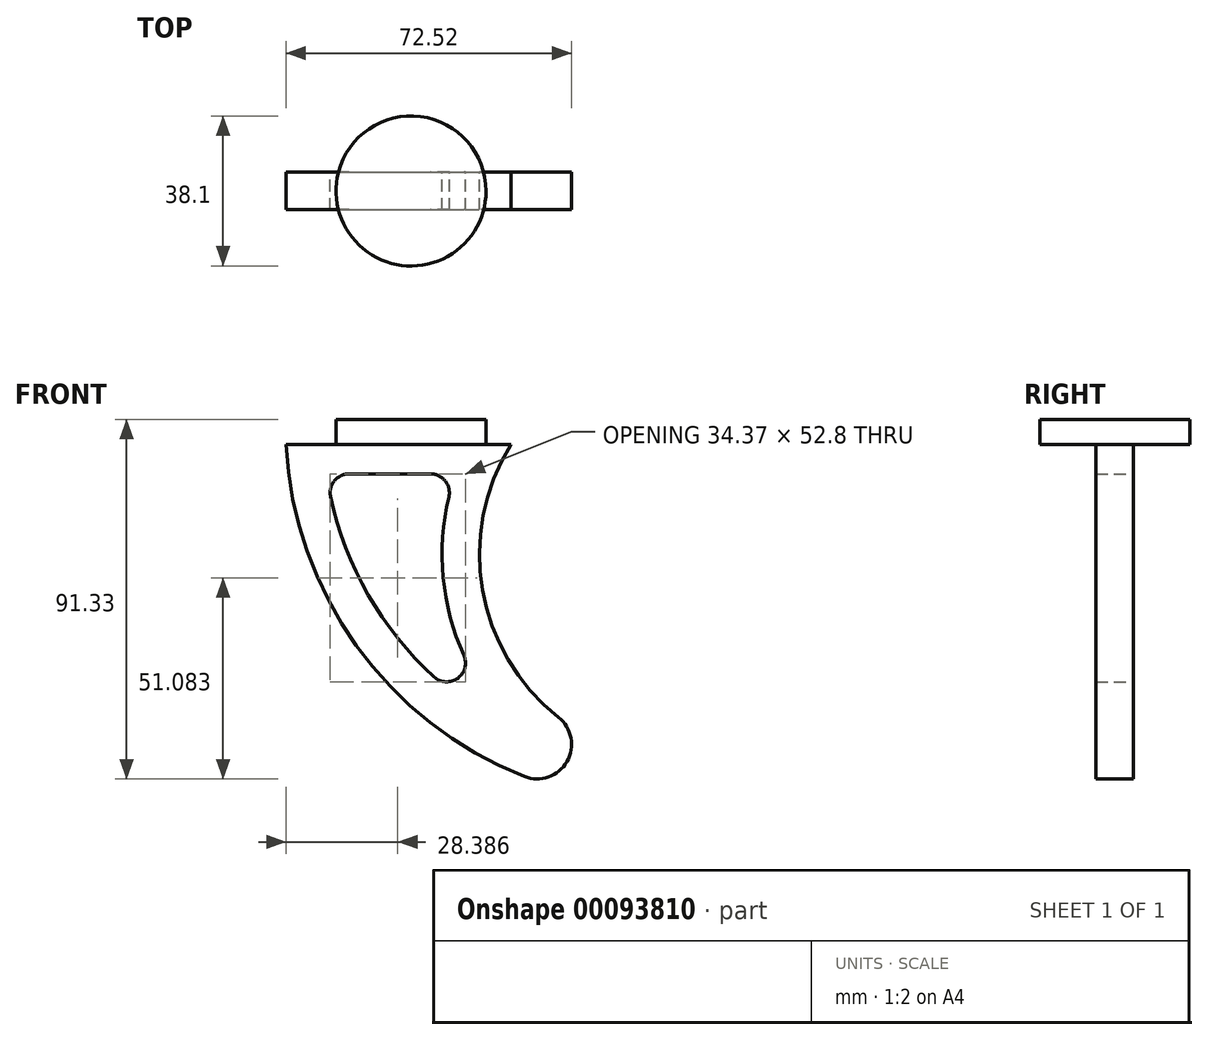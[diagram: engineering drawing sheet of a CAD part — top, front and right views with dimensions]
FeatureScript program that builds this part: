
annotation { "Feature Type Name" : "Feature", "Feature Type Description" : "" }
export const myFeature = defineFeature(function(context is Context, id is Id, definition is map)
    precondition{}
    {
        {
            var Q0;
            Q0=qCreatedBy(makeId("Front.planeOp"),FACE);
            var sketch = newSketch(context, id + "F0", { "sketchPlane" : qUnion([Q0])});
            skLineSegment(sketch, "E0", {"start": v(0, 0) * mm, "end": v(57.15, 0) * mm});
            skArc(sketch, "E1", {"start": v(0, 0) * mm, "mid": v(17.84, -51.1) * mm, "end": v(60.53, -84.37) * mm});
            skArc(sketch, "E2", {"start": v(57.15, 0) * mm, "mid": v(49.94, -36.96) * mm, "end": v(69.2, -69.32) * mm});
            skArc(sketch, "E3", {"start": v(60.53, -84.37) * mm, "mid": v(71.35, -80.58) * mm, "end": v(69.2, -69.32) * mm});
            skLineSegment(sketch, "E4", {"start": v(15.96, -7.5) * mm, "end": v(36.73, -7.5) * mm});
            skArc(sketch, "E5", {"start": v(11.3, -13.25) * mm, "mid": v(20.87, -38.22) * mm, "end": v(37.62, -59.07) * mm});
            skArc(sketch, "E6", {"start": v(41.36, -13.37) * mm, "mid": v(39.91, -33.8) * mm, "end": v(45.16, -53.58) * mm});
            skArc(sketch, "E7", {"start": v(37.62, -59.07) * mm, "mid": v(43.62, -59.4) * mm, "end": v(45.16, -53.58) * mm});
            skPoint(sketch, "E8.visualSharp", {"position": v(10.28, -7.5) * mm});
            skArc(sketch, "E8.filletArc", {"start": v(15.96, -7.5) * mm, "mid": v(12.26, -9.26) * mm, "end": v(11.3, -13.25) * mm});
            skPoint(sketch, "E9.visualSharp", {"position": v(43.08, -7.5) * mm});
            skArc(sketch, "E9.filletArc", {"start": v(41.36, -13.37) * mm, "mid": v(40.47, -9.31) * mm, "end": v(36.73, -7.5) * mm});
            skSolve(sketch);
        }
        {
            var Q0;
            Q0 = qSketchRegion(id + "F0", true);
            extrude(context, id + "F1", {"entities" : qUnion([Q0]), "depth" : 9.52 * mm});
        }
        {
            var Q0;
            Q0=makeQuery(id+"F1.opExtrude","SWEPT_FACE",FACE,{"disambiguationData":[OSD([sQuery(id+"F0.wireOp",EDGE,"E0")])]});
            var sketch = newSketch(context, id + "F2", { "sketchPlane" : qUnion([Q0])});
            skSolve(sketch);
        }
        {
            var Q0;
            {var subQ0=sQuery(id+"F0.wireOp",EDGE,"E0");Q0=makeQuery(id+"F2.imprint","IMPRINT",FACE,{"disambiguationData":[TD([[makeQuery(id+"F2.imprint","IMPRINT",EDGE,{"derivedFrom":makeQuery(id+"F1.opExtrude","CAP_EDGE",EDGE,{"disambiguationData":[OSD([subQ0])],"isStart":true})}),-1.0]])]});}
            var sketch = newSketch(context, id + "F3", { "sketchPlane" : qUnion([Q0])});
            skCircle(sketch, "E10", {"center": v(31.75, -4.76) * mm, "radius": 19.05 * mm});
            skSolve(sketch);
        }
        {
            var Q0;
            Q0 = qSketchRegion(id + "F3", true);
            extrude(context, id + "F4", {"entities" : qUnion([Q0]), "operationType" : NewBodyOperationType.ADD, "depth" : 6.35 * mm});
        }
    });
